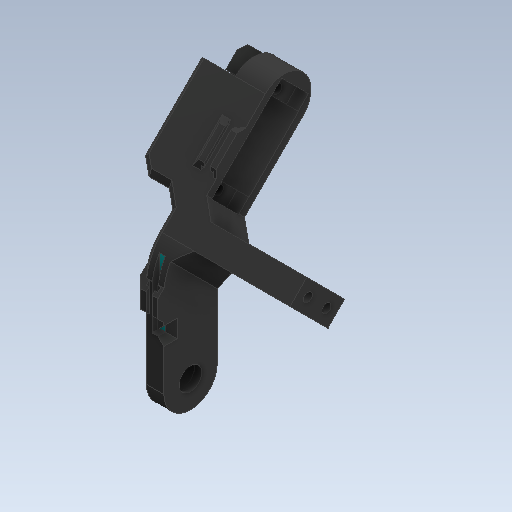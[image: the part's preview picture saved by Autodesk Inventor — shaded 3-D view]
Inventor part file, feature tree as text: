
AUTODESK INVENTOR PART (.ipt)
format: ipt  version: 2020 (Build 240168000, 168)  size: 432,128 bytes
history: native  units: in
note: dims shown in document units (in); Inventor stores cm internally (conversion verified against a paired STEP export)
features: sketch x26, other x7, plane x4
ambient origin geometry x8: Origin, YZ Plane, XZ Plane, XY Plane, X Axis, Y Axis, Z Axis, Center Point
bodies: Solid2 (feature_tree), Solid3 (feature_tree), Solid1 (feature_tree), Solid4 (feature_tree)
feature tree (37):
  other  "PatellaBot.ipt"
  other  "Solid1::PatellaBot.ipt"
  other  "Solid4::PatellaBot.ipt"
  other  "Solid5::PatellaBot.ipt"
  other  "Solid2::PatellaBot.ipt"
  other  "Solid3::PatellaBot.ipt"
  other  "TaggingFeature1"
  sketch  "Sketch1"  dims[d0=0.3937in]
  sketch  "Sketch2"
  sketch  "Sketch3"
  sketch  "Sketch4"
  sketch  "Sketch5"
  sketch  "Sketch12"
  sketch  "Sketch14"
  sketch  "Sketch15"
  sketch  "Sketch16"
  sketch  "Sketch17"
  sketch  "Sketch19"
  sketch  "Sketch22"
  sketch  "Sketch23"
  sketch  "Sketch25"
  sketch  "Sketch26"
  sketch  "Sketch27"
  sketch  "Sketch28"
  sketch  "Sketch32"
  sketch  "Sketch33"
  sketch  "Sketch39"
  sketch  "Sketch40"
  sketch  "Sketch46"
  sketch  "Sketch47"
  sketch  "Sketch48"
  sketch  "Sketch49"
  sketch  "Sketch50"
  plane  "Work Plane1"
  plane  "Work Plane2"
  plane  "Work Plane3"
  plane  "Work Plane4"
